# Revit family: RPC_FSN3_1.5_to_6.0_LOD_200
name_source: partatom
category: Equipement de génie climatique
revit_build: Autodesk Revit 2016 (Build: 20150220_1215(x64)
units: mm (PartAtom-declared; Revit-internal decimal feet)

## family parameters
Cote de connecteur circulaire = Utiliser le diamètre
Couper avec des vides une fois chargée = Non
Hôte = Face
Numéro OmniClass = 23.75.70.00
Partagée = Non
Point de calcul de pièce = Non
Titre OmniClass = HVAC Distribution Devices
Type d'élément = Normal

## types (7) — shared parameters
BC_OBJECT_ID = 6657
Color = Spring white (4.1Y8.5/0.7)
Diamètre Eau Sortie = 25 mm  [stored 0.082021 ft]
Drain distance = 222 mm
Drain pipe Hight = 40 mm  [stored 0.131234 ft]
Elévation par défaut = 1219 mm
Fabricant = HITACHI
Frequency = 50 Hz
Gas distance = 94 mm  [stored 0.308399 ft]
Gas pipe Hight = 107 mm  [stored 0.35105 ft]
Liquid distance = 146 mm  [stored 0.479003 ft]
Liquid pipe Hight = 117 mm  [stored 0.383858 ft]
Maximum AC Voltage = 253 V
Minimum AC Voltage = 207 V
Modèle = RPC FSN3
Nominal Voltage = 230 V
Number of Poles = 1
Overall Depth = 690 mm  [stored 2.26378 ft]
Overall Height = 235 mm  [stored 0.770997 ft]
Refrigerant = R410A (factory-charged corrosion-proof nitrogen)
Usage Current = 5 A

## per-type parameters (varying)
| type | Air Flow(HiH/Hi/Me/low) m3/min | Cooling Capacity | Diamètre Eau Entrée | Diamètre Gaz Entrée | Fan motor type (output) | Heating Capacity | Mass | Maximum Air Flow | Minimum Air Flow | Overall Width | Sound power at minimal load (dB(A)) | Sound power level (dB(A)) | Sound power max (dB(A)) |
| RPC FSN3 1.5 | 15/13/11/9 | 4 kW | 6 mm  [stored 0.019685 ft] | 15 mm  [stored 0.0492126 ft] | 50 W | 4 kW | 26.00 kg | 15000.0 L/min | 9000.0 L/min | 960 mm  [stored 3.14961 ft] | 28 | 53 | 37 |
| RPC FSN3 2.0 | 15/13/11/9 | 5 kW | 6 mm  [stored 0.019685 ft] | 18 mm  [stored 0.0590551 ft] | 50 W | 6 kW | 27.00 kg | 15000.0 L/min | 9000.0 L/min | 960 mm  [stored 3.14961 ft] | 28 | 54 | 38 |
| RPC FSN3 2.5 | 19/16.5/14/11.5 | 6 kW | 10 mm  [stored 0.0328084 ft] | 18 mm  [stored 0.0590551 ft] | 80 W | 6 kW | 35.00 kg | 19000.0 L/min | 11500.0 L/min | 1270 mm | 28 | 54 | 38 |
| RPC FSN3 3.0 | 21/18.5/15.5/12.5 | 7 kW | 10 mm  [stored 0.0328084 ft] | 18 mm  [stored 0.0590551 ft] | 80 W | 8 kW | 35.00 kg | 21000.0 L/min | 12500.0 L/min | 1270 mm | 29 | 56 | 40 |
| RPC FSN3 6.0 | 37/32.5/27/21 | 14 kW | 10 mm  [stored 0.0328084 ft] | 18 mm  [stored 0.0590551 ft] | 160 W | 16 kW | 41.00 kg | 37000.0 L/min | 21000.0 L/min | 1580 mm  [stored 5.18373 ft] | 36 | 65 | 49 |
| RPC FSN3 5.0 | 35/31/25.5/20 | 13 kW | 10 mm  [stored 0.0328084 ft] | 18 mm  [stored 0.0590551 ft] | 160 W | 14 kW | 41.00 kg | 35000.0 L/min | 20000.0 L/min | 1580 mm  [stored 5.18373 ft] | 35 | 64 | 48 |
| RPC FSN3 4.0 | 30/26.5/22/17 | 10 kW | 10 mm  [stored 0.0328084 ft] | 18 mm  [stored 0.0590551 ft] | 160 W | 11 kW | 41.00 kg | 30000.0 L/min | 17000.0 L/min | 1580 mm  [stored 5.18373 ft] | 32 | 60 | 44 |

note: [stored X ft] marks values corroborated as IEEE doubles in the binary element streams (Revit-internal decimal feet)

## geometry (parser evidence)
native form markers: Blend x2
no freeform markers — native parametric forms only
